# Revit family: Скамейка стальная «Пифагор» Арт 10895
name_source: partatom
category: Антураж
revit_build: Autodesk Revit 2018 (Build: 20180423_1000(x64)
units: mm (PartAtom-declared; Revit-internal decimal feet)

## family parameters
Всегда вертикально = Да
Источник визуального образа = Геометрия семейства
На основе рабочей плоскости = Нет
Общий = Нет
При загрузке вырезать с полостями = Нет
Точка расчета площади = Нет

## types (8) — shared parameters
URL = https://hobbyka.ru
Артикул товара = Арт. 10895
Высота = 1319 мм
Группа модели = Скамейки
Изготовитель = ООО «Хоббика»
Описание = Сталь, дерево
Цвет опоры = Сталь
Цвет отделки = Дерево
Ширина = 1211 мм

## per-type parameters (varying)
| type | Версия 1,2 м | Версия 1,5 м | Версия 1,8 м | Версия 2,0 м | Версия 2,5 м | Версия 3,0 м | Длина | Изображение типоразмера | Материал изделия | С большим разделителем | С маленьким разделителем | Средняя опора |
| Версия 1,2 м | Да | Нет | Нет | Нет | Нет | Нет | 1200 мм | Скамейка стальная «Пифагор» Арт 10895 1,2 м.jpg | Скамейка стальная «Пифагор». Версия 1,2 м | Нет | Нет | Нет |
| Версия 1,5 м | Нет | Да | Нет | Нет | Нет | Нет | 1500 мм | Скамейка стальная «Пифагор» Арт 10895 1,5 м.jpg | Скамейка стальная «Пифагор». Версия 1,5 м | Нет | Нет | Нет |
| Версия 1,8 м | Нет | Нет | Да | Нет | Нет | Нет | 1800 мм | Скамейка стальная «Пифагор» Арт 10895 1,8 м.jpg | Скамейка стальная «Пифагор». Версия 1,8 м. С тремя опорами | Нет | Нет | Да |
| Версия 2,0 м | Нет | Нет | Нет | Да | Нет | Нет | 2000 мм | Скамейка стальная «Пифагор» Арт 10895 2,0 м.jpg | Скамейка стальная «Пифагор». Версия 2,0 м. С тремя опорами | Нет | Нет | Да |
| Версия 2,5 м | Нет | Нет | Нет | Нет | Да | Нет | 2500 мм | Скамейка стальная «Пифагор» Арт 10895 3 опоры.jpg | Скамейка стальная «Пифагор». Версия 2,5 м. С тремя опорами | Нет | Нет | Да |
| Версия 3,0 м | Нет | Нет | Нет | Нет | Нет | Да | 3000 мм | Скамейка стальная «Пифагор» Арт 10895 3 опоры.jpg | Скамейка стальная «Пифагор». Версия 3,0 м. С тремя опорами | Нет | Нет | Да |
| С большиими разделителями | Нет | Нет | Нет | Нет | Нет | Нет | 3000 мм | Скамейка стальная «Пифагор» Арт 10895 с большим разделителем.jpg | Скамейка стальная «Пифагор». Версия 3,0 м. С тремя опорами и большими разделителями | Да | Нет | Да |
| С маленькими разделителями | Нет | Нет | Нет | Нет | Нет | Нет | 3000 мм | Скамейка стальная «Пифагор» Арт 10895 с маленьким разделителем.jpg | Скамейка стальная «Пифагор». Версия 3,0 м. С тремя опорами и маленькими разделителями | Нет | Да | Да |
